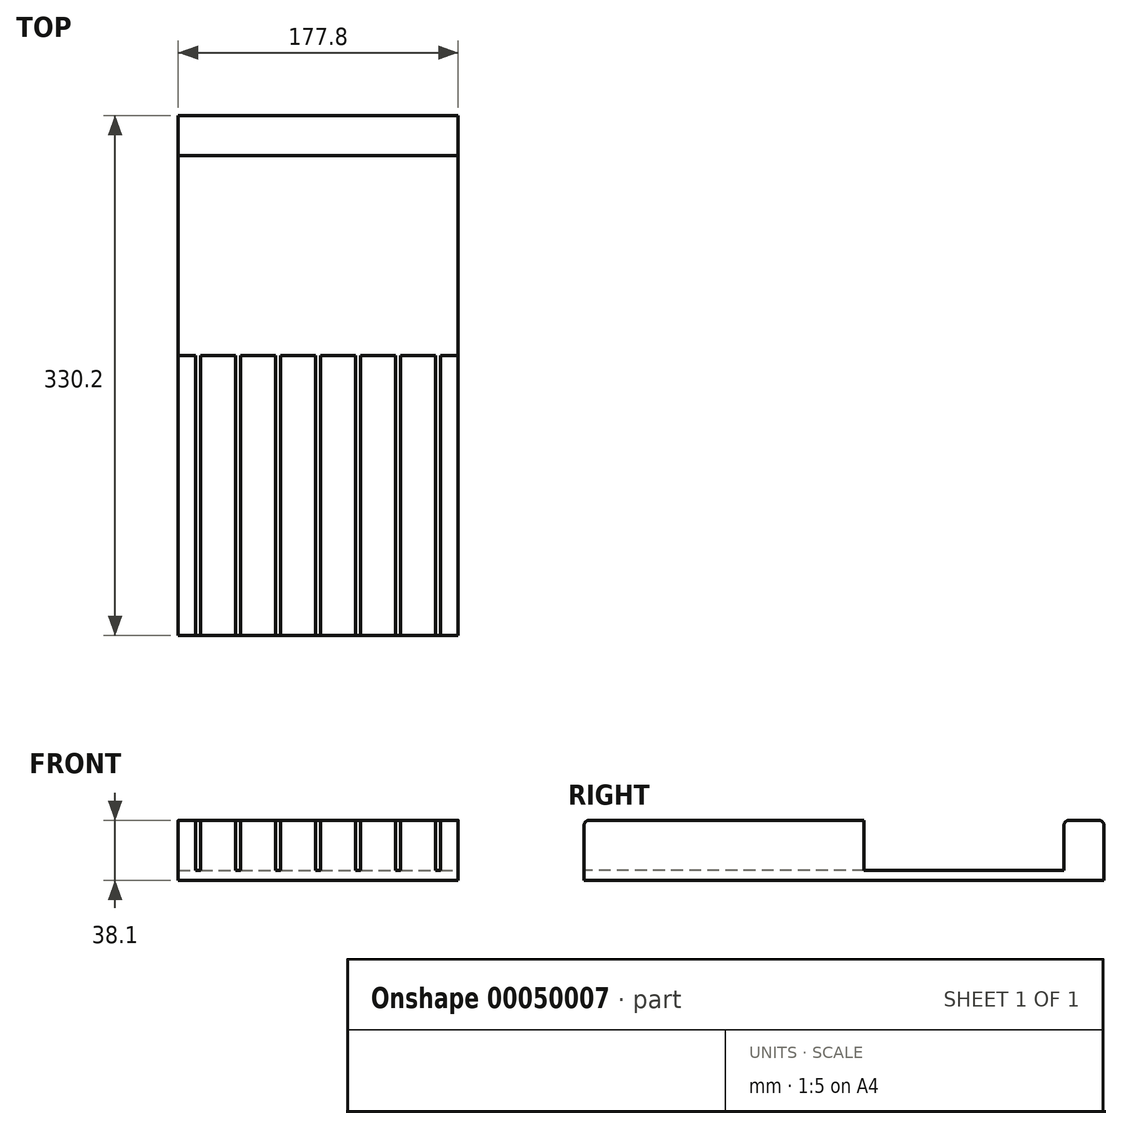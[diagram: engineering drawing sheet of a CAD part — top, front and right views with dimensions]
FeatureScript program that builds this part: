
annotation { "Feature Type Name" : "Feature", "Feature Type Description" : "" }
export const myFeature = defineFeature(function(context is Context, id is Id, definition is map)
    precondition{}
    {
        {
            var Q0;
            Q0=qCreatedBy(makeId("Top.planeOp"),FACE);
            var sketch = newSketch(context, id + "F0", { "sketchPlane" : qUnion([Q0])});
            skLineSegment(sketch, "E0.bottom", {"start": v(-161.67, 165.4) * mm, "end": v(16.13, 165.4) * mm});
            skLineSegment(sketch, "E0.top", {"start": v(-161.67, -164.8) * mm, "end": v(16.13, -164.8) * mm});
            skLineSegment(sketch, "E0.left", {"start": v(-161.67, 165.4) * mm, "end": v(-161.67, -164.8) * mm});
            skLineSegment(sketch, "E0.right", {"start": v(16.13, 165.4) * mm, "end": v(16.13, -164.8) * mm});
            skSolve(sketch);
        }
        {
            var Q0;
            Q0=makeQuery(id+"F0.imprint","IMPRINT",FACE,{"disambiguationData":[TD([[makeQuery(id+"F0.imprint","IMPRINT",EDGE,{"derivedFrom":sQuery(id+"F0.wireOp",EDGE,"E0.bottom")}),-1.0]])]});
            extrude(context, id + "F1", {"entities" : qUnion([Q0]), "depth" : 38.1 * mm});
        }
        {
            var Q0;
            Q0=makeQuery(id+"F1.opExtrude","CAP_FACE",FACE,{"disambiguationData":[OSD([sQuery(id+"F0.wireOp",EDGE,"E0.bottom"),sQuery(id+"F0.wireOp",EDGE,"E0.top"),sQuery(id+"F0.wireOp",EDGE,"E0.left"),sQuery(id+"F0.wireOp",EDGE,"E0.right")])],"isStart":false});
            var sketch = newSketch(context, id + "F2", { "sketchPlane" : qUnion([Q0])});
            skLineSegment(sketch, "E1", {"start": v(-161.67, 140) * mm, "end": v(16.13, 140) * mm});
            skLineSegment(sketch, "E2", {"start": v(-161.67, 13) * mm, "end": v(16.13, 13) * mm});
            skSolve(sketch);
        }
        {
            var Q0;
            {var subQ2=sQuery(id+"F2.wireOp",EDGE,"E1");Q0=makeQuery(id+"F2.imprint","IMPRINT",FACE,{"disambiguationData":[TD([[makeQuery(id+"F2.imprint","IMPRINT",EDGE,{"derivedFrom":subQ2}),-1.0]])]});}
            extrude(context, id + "F3", {"entities" : qUnion([Q0]), "operationType" : NewBodyOperationType.REMOVE, "oppositeDirection" : true, "depth" : 31.75 * mm});
        }
        {
            var Q0;
            {var subQ0=sQuery(id+"F0.wireOp",EDGE,"E0.top");var subQ1=sQuery(id+"F0.wireOp",EDGE,"E0.left");var subQ2=sQuery(id+"F0.wireOp",EDGE,"E0.right");Q0=makeQuery(id+"F3.boolean.opBoolean","SPLIT",FACE,{"disambiguationData":[TD([makeQuery(id+"F1.opExtrude","SWEPT_FACE",FACE,{"disambiguationData":[OSD([subQ0])]})])],"derivedFrom":makeQuery(id+"F1.opExtrude","CAP_FACE",FACE,{"disambiguationData":[OSD([sQuery(id+"F0.wireOp",EDGE,"E0.bottom"),subQ0,subQ1,subQ2])],"isStart":false})});}
            var sketch = newSketch(context, id + "F4", { "sketchPlane" : qUnion([Q0])});
            skLineSegment(sketch, "E3", {"start": v(-150.55, 13) * mm, "end": v(-150.55, -164.8) * mm});
            skLineSegment(sketch, "E4", {"start": v(-147.38, 13) * mm, "end": v(-147.38, -164.8) * mm});
            skLineSegment(sketch, "E5.1.0.0", {"start": v(-125.15, 13) * mm, "end": v(-125.15, -164.8) * mm});
            skLineSegment(sketch, "E5.1.0.1", {"start": v(-121.98, 13) * mm, "end": v(-121.98, -164.8) * mm});
            skLineSegment(sketch, "E5.2.0.0", {"start": v(-99.75, 13) * mm, "end": v(-99.75, -164.8) * mm});
            skLineSegment(sketch, "E5.2.0.1", {"start": v(-96.58, 13) * mm, "end": v(-96.58, -164.8) * mm});
            skLineSegment(sketch, "E5.3.0.0", {"start": v(-74.35, 13) * mm, "end": v(-74.35, -164.8) * mm});
            skLineSegment(sketch, "E5.3.0.1", {"start": v(-71.18, 13) * mm, "end": v(-71.18, -164.8) * mm});
            skLineSegment(sketch, "E5.4.0.0", {"start": v(-48.95, 13) * mm, "end": v(-48.95, -164.8) * mm});
            skLineSegment(sketch, "E5.4.0.1", {"start": v(-45.78, 13) * mm, "end": v(-45.78, -164.8) * mm});
            skLineSegment(sketch, "E5.5.0.0", {"start": v(-23.55, 13) * mm, "end": v(-23.55, -164.8) * mm});
            skLineSegment(sketch, "E5.5.0.1", {"start": v(-20.38, 13) * mm, "end": v(-20.38, -164.8) * mm});
            skLineSegment(sketch, "E5.6.0.0", {"start": v(1.85, 13) * mm, "end": v(1.85, -164.8) * mm});
            skLineSegment(sketch, "E5.6.0.1", {"start": v(5.02, 13) * mm, "end": v(5.02, -164.8) * mm});
            skLineSegment(sketch, "E5.direction1", {"start": v(-147.38, -164.8) * mm, "end": v(-121.98, -164.8) * mm, "construction": true});
            skSolve(sketch);
        }
        {
            var Q0;
            {var subQ2=sQuery(id+"F4.wireOp",EDGE,"E3");Q0=makeQuery(id+"F4.imprint","IMPRINT",FACE,{"disambiguationData":[TD([[makeQuery(id+"F4.imprint","IMPRINT",EDGE,{"derivedFrom":subQ2}),1.0]])]});}
            var Q1;
            {var subQ2=sQuery(id+"F4.wireOp",EDGE,"E5.1.0.0");Q1=makeQuery(id+"F4.imprint","IMPRINT",FACE,{"disambiguationData":[TD([[makeQuery(id+"F4.imprint","IMPRINT",EDGE,{"derivedFrom":subQ2}),1.0]])]});}
            var Q2;
            {var subQ2=sQuery(id+"F4.wireOp",EDGE,"E5.2.0.0");Q2=makeQuery(id+"F4.imprint","IMPRINT",FACE,{"disambiguationData":[TD([[makeQuery(id+"F4.imprint","IMPRINT",EDGE,{"derivedFrom":subQ2}),1.0]])]});}
            var Q3;
            {var subQ2=sQuery(id+"F4.wireOp",EDGE,"E5.3.0.0");Q3=makeQuery(id+"F4.imprint","IMPRINT",FACE,{"disambiguationData":[TD([[makeQuery(id+"F4.imprint","IMPRINT",EDGE,{"derivedFrom":subQ2}),1.0]])]});}
            var Q4;
            {var subQ2=sQuery(id+"F4.wireOp",EDGE,"E5.4.0.0");Q4=makeQuery(id+"F4.imprint","IMPRINT",FACE,{"disambiguationData":[TD([[makeQuery(id+"F4.imprint","IMPRINT",EDGE,{"derivedFrom":subQ2}),1.0]])]});}
            var Q5;
            {var subQ2=sQuery(id+"F4.wireOp",EDGE,"E5.5.0.0");Q5=makeQuery(id+"F4.imprint","IMPRINT",FACE,{"disambiguationData":[TD([[makeQuery(id+"F4.imprint","IMPRINT",EDGE,{"derivedFrom":subQ2}),1.0]])]});}
            var Q6;
            {var subQ2=sQuery(id+"F4.wireOp",EDGE,"E5.6.0.0");Q6=makeQuery(id+"F4.imprint","IMPRINT",FACE,{"disambiguationData":[TD([[makeQuery(id+"F4.imprint","IMPRINT",EDGE,{"derivedFrom":subQ2}),1.0]])]});}
            extrude(context, id + "F5", {"entities" : qUnion([Q0, Q1, Q2, Q3, Q4, Q5, Q6]), "operationType" : NewBodyOperationType.REMOVE, "oppositeDirection" : true, "depth" : 31.75 * mm});
        }
        {
            var Q0;
            Q0=makeQuery(id+"F3.boolean.opBoolean","COPY",EDGE,{"derivedFrom":makeQuery(id+"F3.opExtrude","CAP_EDGE",EDGE,{"disambiguationData":[OSD([sQuery(id+"F2.wireOp",EDGE,"E1")])],"isStart":true})});
            var Q1;
            {var subQ0=sQuery(id+"F0.wireOp",EDGE,"E0.top");Q1=makeQuery(id+"F5.boolean.opBoolean","SPLIT",EDGE,{"disambiguationData":[TD([makeQuery(id+"F5.opExtrude","SWEPT_FACE",FACE,{"disambiguationData":[OSD([sQuery(id+"F4.wireOp",EDGE,"E4")])]})])],"derivedFrom":makeQuery(id+"F1.opExtrude","CAP_EDGE",EDGE,{"disambiguationData":[OSD([subQ0])],"isStart":false})});}
            var Q2;
            {var subQ0=sQuery(id+"F0.wireOp",EDGE,"E0.top");Q2=makeQuery(id+"F5.boolean.opBoolean","SPLIT",EDGE,{"disambiguationData":[TD([makeQuery(id+"F5.opExtrude","SWEPT_FACE",FACE,{"disambiguationData":[OSD([sQuery(id+"F4.wireOp",EDGE,"E5.1.0.1")])]})])],"derivedFrom":makeQuery(id+"F1.opExtrude","CAP_EDGE",EDGE,{"disambiguationData":[OSD([subQ0])],"isStart":false})});}
            var Q3;
            {var subQ0=sQuery(id+"F0.wireOp",EDGE,"E0.top");Q3=makeQuery(id+"F5.boolean.opBoolean","SPLIT",EDGE,{"disambiguationData":[TD([makeQuery(id+"F5.opExtrude","SWEPT_FACE",FACE,{"disambiguationData":[OSD([sQuery(id+"F4.wireOp",EDGE,"E5.2.0.1")])]})])],"derivedFrom":makeQuery(id+"F1.opExtrude","CAP_EDGE",EDGE,{"disambiguationData":[OSD([subQ0])],"isStart":false})});}
            var Q4;
            {var subQ0=sQuery(id+"F0.wireOp",EDGE,"E0.top");var subQ1=sQuery(id+"F0.wireOp",EDGE,"E0.left");Q4=makeQuery(id+"F5.boolean.opBoolean","SPLIT",EDGE,{"disambiguationData":[TD([makeQuery(id+"F1.opExtrude","SWEPT_FACE",FACE,{"disambiguationData":[OSD([subQ1])]})])],"derivedFrom":makeQuery(id+"F1.opExtrude","CAP_EDGE",EDGE,{"disambiguationData":[OSD([subQ0])],"isStart":false})});}
            var Q5;
            {var subQ0=sQuery(id+"F0.wireOp",EDGE,"E0.top");Q5=makeQuery(id+"F5.boolean.opBoolean","SPLIT",EDGE,{"disambiguationData":[TD([makeQuery(id+"F5.opExtrude","SWEPT_FACE",FACE,{"disambiguationData":[OSD([sQuery(id+"F4.wireOp",EDGE,"E5.3.0.1")])]})])],"derivedFrom":makeQuery(id+"F1.opExtrude","CAP_EDGE",EDGE,{"disambiguationData":[OSD([subQ0])],"isStart":false})});}
            var Q6;
            {var subQ0=sQuery(id+"F0.wireOp",EDGE,"E0.top");Q6=makeQuery(id+"F5.boolean.opBoolean","SPLIT",EDGE,{"disambiguationData":[TD([makeQuery(id+"F5.opExtrude","SWEPT_FACE",FACE,{"disambiguationData":[OSD([sQuery(id+"F4.wireOp",EDGE,"E5.4.0.1")])]})])],"derivedFrom":makeQuery(id+"F1.opExtrude","CAP_EDGE",EDGE,{"disambiguationData":[OSD([subQ0])],"isStart":false})});}
            var Q7;
            {var subQ0=sQuery(id+"F0.wireOp",EDGE,"E0.top");Q7=makeQuery(id+"F5.boolean.opBoolean","SPLIT",EDGE,{"disambiguationData":[TD([makeQuery(id+"F5.opExtrude","SWEPT_FACE",FACE,{"disambiguationData":[OSD([sQuery(id+"F4.wireOp",EDGE,"E5.5.0.1")])]})])],"derivedFrom":makeQuery(id+"F1.opExtrude","CAP_EDGE",EDGE,{"disambiguationData":[OSD([subQ0])],"isStart":false})});}
            var Q8;
            {var subQ0=sQuery(id+"F0.wireOp",EDGE,"E0.top");var subQ1=sQuery(id+"F0.wireOp",EDGE,"E0.right");Q8=makeQuery(id+"F5.boolean.opBoolean","SPLIT",EDGE,{"disambiguationData":[TD([makeQuery(id+"F1.opExtrude","SWEPT_FACE",FACE,{"disambiguationData":[OSD([subQ1])]})])],"derivedFrom":makeQuery(id+"F1.opExtrude","CAP_EDGE",EDGE,{"disambiguationData":[OSD([subQ0])],"isStart":false})});}
            var Q9;
            {var subQ0=sQuery(id+"F2.wireOp",EDGE,"E2");var subQ1=sQuery(id+"F0.wireOp",EDGE,"E0.left");Q9=makeQuery(id+"F5.boolean.opBoolean","SPLIT",EDGE,{"disambiguationData":[TD([makeQuery(id+"F1.opExtrude","SWEPT_FACE",FACE,{"disambiguationData":[OSD([subQ1])]})])],"derivedFrom":makeQuery(id+"F3.boolean.opBoolean","COPY",EDGE,{"derivedFrom":makeQuery(id+"F3.opExtrude","CAP_EDGE",EDGE,{"disambiguationData":[OSD([subQ0])],"isStart":true})})});}
            var Q10;
            {var subQ0=sQuery(id+"F2.wireOp",EDGE,"E2");Q10=makeQuery(id+"F5.boolean.opBoolean","SPLIT",EDGE,{"disambiguationData":[TD([makeQuery(id+"F5.opExtrude","SWEPT_FACE",FACE,{"disambiguationData":[OSD([sQuery(id+"F4.wireOp",EDGE,"E4")])]})])],"derivedFrom":makeQuery(id+"F3.boolean.opBoolean","COPY",EDGE,{"derivedFrom":makeQuery(id+"F3.opExtrude","CAP_EDGE",EDGE,{"disambiguationData":[OSD([subQ0])],"isStart":true})})});}
            var Q11;
            {var subQ0=sQuery(id+"F2.wireOp",EDGE,"E2");Q11=makeQuery(id+"F5.boolean.opBoolean","SPLIT",EDGE,{"disambiguationData":[TD([makeQuery(id+"F5.opExtrude","SWEPT_FACE",FACE,{"disambiguationData":[OSD([sQuery(id+"F4.wireOp",EDGE,"E5.1.0.1")])]})])],"derivedFrom":makeQuery(id+"F3.boolean.opBoolean","COPY",EDGE,{"derivedFrom":makeQuery(id+"F3.opExtrude","CAP_EDGE",EDGE,{"disambiguationData":[OSD([subQ0])],"isStart":true})})});}
            var Q12;
            {var subQ0=sQuery(id+"F2.wireOp",EDGE,"E2");Q12=makeQuery(id+"F5.boolean.opBoolean","SPLIT",EDGE,{"disambiguationData":[TD([makeQuery(id+"F5.opExtrude","SWEPT_FACE",FACE,{"disambiguationData":[OSD([sQuery(id+"F4.wireOp",EDGE,"E5.2.0.1")])]})])],"derivedFrom":makeQuery(id+"F3.boolean.opBoolean","COPY",EDGE,{"derivedFrom":makeQuery(id+"F3.opExtrude","CAP_EDGE",EDGE,{"disambiguationData":[OSD([subQ0])],"isStart":true})})});}
            var Q13;
            {var subQ0=sQuery(id+"F2.wireOp",EDGE,"E2");Q13=makeQuery(id+"F5.boolean.opBoolean","SPLIT",EDGE,{"disambiguationData":[TD([makeQuery(id+"F5.opExtrude","SWEPT_FACE",FACE,{"disambiguationData":[OSD([sQuery(id+"F4.wireOp",EDGE,"E5.3.0.1")])]})])],"derivedFrom":makeQuery(id+"F3.boolean.opBoolean","COPY",EDGE,{"derivedFrom":makeQuery(id+"F3.opExtrude","CAP_EDGE",EDGE,{"disambiguationData":[OSD([subQ0])],"isStart":true})})});}
            var Q14;
            {var subQ0=sQuery(id+"F2.wireOp",EDGE,"E2");Q14=makeQuery(id+"F5.boolean.opBoolean","SPLIT",EDGE,{"disambiguationData":[TD([makeQuery(id+"F5.opExtrude","SWEPT_FACE",FACE,{"disambiguationData":[OSD([sQuery(id+"F4.wireOp",EDGE,"E5.4.0.1")])]})])],"derivedFrom":makeQuery(id+"F3.boolean.opBoolean","COPY",EDGE,{"derivedFrom":makeQuery(id+"F3.opExtrude","CAP_EDGE",EDGE,{"disambiguationData":[OSD([subQ0])],"isStart":true})})});}
            var Q15;
            {var subQ0=sQuery(id+"F2.wireOp",EDGE,"E2");Q15=makeQuery(id+"F5.boolean.opBoolean","SPLIT",EDGE,{"disambiguationData":[TD([makeQuery(id+"F5.opExtrude","SWEPT_FACE",FACE,{"disambiguationData":[OSD([sQuery(id+"F4.wireOp",EDGE,"E5.5.0.1")])]})])],"derivedFrom":makeQuery(id+"F3.boolean.opBoolean","COPY",EDGE,{"derivedFrom":makeQuery(id+"F3.opExtrude","CAP_EDGE",EDGE,{"disambiguationData":[OSD([subQ0])],"isStart":true})})});}
            var Q16;
            {var subQ0=sQuery(id+"F2.wireOp",EDGE,"E2");var subQ1=sQuery(id+"F0.wireOp",EDGE,"E0.right");Q16=makeQuery(id+"F5.boolean.opBoolean","SPLIT",EDGE,{"disambiguationData":[TD([makeQuery(id+"F1.opExtrude","SWEPT_FACE",FACE,{"disambiguationData":[OSD([subQ1])]})])],"derivedFrom":makeQuery(id+"F3.boolean.opBoolean","COPY",EDGE,{"derivedFrom":makeQuery(id+"F3.opExtrude","CAP_EDGE",EDGE,{"disambiguationData":[OSD([subQ0])],"isStart":true})})});}
            var Q17;
            Q17=makeQuery(id+"F1.opExtrude","CAP_EDGE",EDGE,{"disambiguationData":[OSD([sQuery(id+"F0.wireOp",EDGE,"E0.bottom")])],"isStart":false});
            fillet(context, id + "F6", {"entities" : qUnion([Q0, Q1, Q2, Q3, Q4, Q5, Q6, Q7, Q8, Q9, Q10, Q11, Q12, Q13, Q14, Q15, Q16, Q17]), "radius" : 3.17 * mm, "tangentPropagation" : true, "allowEdgeOverflow" : false});
        }
    });
